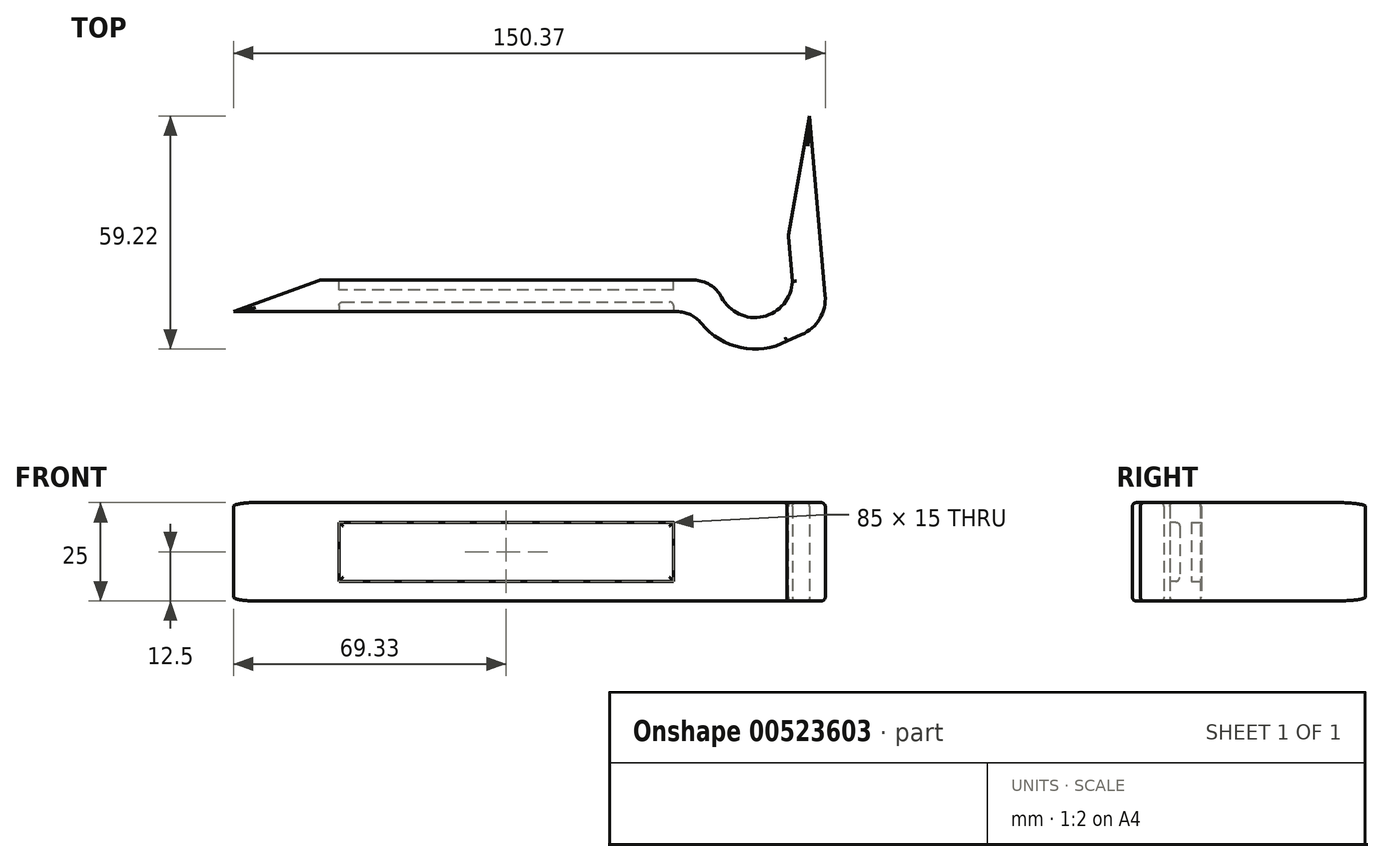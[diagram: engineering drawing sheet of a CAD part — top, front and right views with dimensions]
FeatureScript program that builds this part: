
annotation { "Feature Type Name" : "Feature", "Feature Type Description" : "" }
export const myFeature = defineFeature(function(context is Context, id is Id, definition is map)
    precondition{}
    {
        {
            var Q0;
            Q0=qCreatedBy(makeId("Top.planeOp"),FACE);
            var sketch = newSketch(context, id + "F0", { "sketchPlane" : qUnion([Q0])});
            skLineSegment(sketch, "E0.bottom", {"start": v(-48.85, 1.55) * mm, "end": v(46.1, 1.55) * mm});
            skLineSegment(sketch, "E0.top", {"start": v(-70.83, -6.45) * mm, "end": v(41.82, -6.45) * mm});
            skLineSegment(sketch, "E1", {"start": v(-70.83, -6.45) * mm, "end": v(-48.85, 1.55) * mm});
            skArc(sketch, "E2", {"start": v(48.05, -9.43) * mm, "mid": v(58.13, -15.59) * mm, "end": v(69.83, -13.93) * mm});
            skArc(sketch, "E3.0", {"start": v(53.22, -2.8) * mm, "mid": v(63.9, -7.68) * mm, "end": v(71.17, 1.55) * mm});
            skPoint(sketch, "E4.visualSharp", {"position": v(52.17, 1.55) * mm});
            skArc(sketch, "E4.filletArc", {"start": v(53.22, -2.8) * mm, "mid": v(50.28, 0.38) * mm, "end": v(46.1, 1.55) * mm});
            skArc(sketch, "E5.filletArc", {"start": v(48.05, -9.43) * mm, "mid": v(45.27, -7.23) * mm, "end": v(41.82, -6.45) * mm});
            skLineSegment(sketch, "E6", {"start": v(79.5, -2.27) * mm, "end": v(75.52, 43.27) * mm});
            skLineSegment(sketch, "E7", {"start": v(67.5, -14.95) * mm, "end": v(73.55, -12.3) * mm});
            skLineSegment(sketch, "E8.0", {"start": v(71.17, 1.25) * mm, "end": v(70.15, 12.83) * mm});
            skPoint(sketch, "E9.visualSharp", {"position": v(80.13, -9.43) * mm});
            skArc(sketch, "E9.filletArc", {"start": v(73.55, -12.3) * mm, "mid": v(78.14, -8.25) * mm, "end": v(79.5, -2.27) * mm});
            skLineSegment(sketch, "E10", {"start": v(75.52, 43.27) * mm, "end": v(70.15, 12.83) * mm});
            skSolve(sketch);
        }
        {
            var Q0;
            Q0 = qSketchRegion(id + "F0", true);
            extrude(context, id + "F1", {"entities" : qUnion([Q0]), "depth" : 25 * mm, "offsetDistance" : 25 * mm});
        }
        {
            var Q0;
            Q0=makeQuery(id+"F1.opExtrude","SWEPT_FACE",FACE,{"disambiguationData":[OSD([sQuery(id+"F0.wireOp",EDGE,"E0.bottom")])]});
            var sketch = newSketch(context, id + "F2", { "sketchPlane" : qUnion([Q0])});
            skLineSegment(sketch, "E11.0", {"start": v(-41, 20) * mm, "end": v(44, 20) * mm});
            skLineSegment(sketch, "E11.1", {"start": v(-41, 20) * mm, "end": v(-41, 5) * mm});
            skLineSegment(sketch, "E11.2", {"start": v(-41, 5) * mm, "end": v(44, 5) * mm});
            skLineSegment(sketch, "E11.3", {"start": v(44, 20) * mm, "end": v(44, 5) * mm});
            skSolve(sketch);
        }
        {
            var Q0;
            Q0 = qSketchRegion(id + "F2", true);
            extrude(context, id + "F3", {"entities" : qUnion([Q0]), "operationType" : NewBodyOperationType.REMOVE, "oppositeDirection" : true, "depth" : 2.5 * mm, "offsetDistance" : 25 * mm});
        }
        {
            var Q0;
            Q0=makeQuery(id+"F1.opExtrude","SWEPT_FACE",FACE,{"disambiguationData":[OSD([sQuery(id+"F0.wireOp",EDGE,"E0.top")])]});
            var sketch = newSketch(context, id + "F4", { "sketchPlane" : qUnion([Q0])});
            skLineSegment(sketch, "E12.bottom", {"start": v(-44, 20) * mm, "end": v(41, 20) * mm});
            skLineSegment(sketch, "E12.top", {"start": v(-44, 5) * mm, "end": v(41, 5) * mm});
            skLineSegment(sketch, "E12.left", {"start": v(-44, 20) * mm, "end": v(-44, 5) * mm});
            skLineSegment(sketch, "E12.right", {"start": v(41, 20) * mm, "end": v(41, 5) * mm});
            skSolve(sketch);
        }
        {
            var Q0;
            Q0 = qSketchRegion(id + "F4", true);
            extrude(context, id + "F5", {"entities" : qUnion([Q0]), "operationType" : NewBodyOperationType.REMOVE, "oppositeDirection" : true, "depth" : 2.5 * mm, "offsetDistance" : 25 * mm});
        }
        {
            var Q0;
            Q0=makeQuery(id+"F1.opExtrude","CAP_EDGE",EDGE,{"disambiguationData":[OSD([sQuery(id+"F0.wireOp",EDGE,"E0.bottom")])],"isStart":true});
            var Q1;
            Q1=makeQuery(id+"F1.opExtrude","CAP_EDGE",EDGE,{"disambiguationData":[OSD([sQuery(id+"F0.wireOp",EDGE,"E8.0")])],"isStart":true});
            var Q2;
            Q2=makeQuery(id+"F1.opExtrude","SWEPT_EDGE",EDGE,{"disambiguationData":[OSD([sQuery(id+"F0.wireOp",EDGE,"E8.0"),sQuery(id+"F0.wireOp",EDGE,"E10")])]});
            var Q3;
            Q3=makeQuery(id+"F1.opExtrude","CAP_EDGE",EDGE,{"disambiguationData":[OSD([sQuery(id+"F0.wireOp",EDGE,"E8.0")])],"isStart":false});
            var Q4;
            Q4=makeQuery(id+"F1.opExtrude","CAP_EDGE",EDGE,{"disambiguationData":[OSD([sQuery(id+"F0.wireOp",EDGE,"E3.0")])],"isStart":false});
            var Q5;
            Q5=makeQuery(id+"F1.opExtrude","SWEPT_EDGE",EDGE,{"disambiguationData":[OSD([sQuery(id+"F0.wireOp",EDGE,"E0.bottom"),sQuery(id+"F0.wireOp",EDGE,"E1")])]});
            var Q6;
            Q6=makeQuery(id+"F3.boolean.opBoolean","COPY",EDGE,{"derivedFrom":makeQuery(id+"F3.opExtrude","CAP_EDGE",EDGE,{"disambiguationData":[OSD([sQuery(id+"F2.wireOp",EDGE,"E11.3")])],"isStart":true})});
            var Q7;
            Q7=makeQuery(id+"F3.boolean.opBoolean","COPY",EDGE,{"derivedFrom":makeQuery(id+"F3.opExtrude","CAP_EDGE",EDGE,{"disambiguationData":[OSD([sQuery(id+"F2.wireOp",EDGE,"E11.2")])],"isStart":true})});
            var Q8;
            Q8=makeQuery(id+"F3.boolean.opBoolean","COPY",EDGE,{"derivedFrom":makeQuery(id+"F3.opExtrude","CAP_EDGE",EDGE,{"disambiguationData":[OSD([sQuery(id+"F2.wireOp",EDGE,"E11.1")])],"isStart":true})});
            var Q9;
            Q9=makeQuery(id+"F3.boolean.opBoolean","COPY",EDGE,{"derivedFrom":makeQuery(id+"F3.opExtrude","CAP_EDGE",EDGE,{"disambiguationData":[OSD([sQuery(id+"F2.wireOp",EDGE,"E11.0")])],"isStart":true})});
            var Q10;
            Q10=makeQuery(id+"F1.opExtrude","CAP_EDGE",EDGE,{"disambiguationData":[OSD([sQuery(id+"F0.wireOp",EDGE,"E0.top")])],"isStart":false});
            var Q11;
            Q11=makeQuery(id+"F1.opExtrude","CAP_EDGE",EDGE,{"disambiguationData":[OSD([sQuery(id+"F0.wireOp",EDGE,"E1")])],"isStart":true});
            var Q12;
            Q12=makeQuery(id+"F1.opExtrude","CAP_EDGE",EDGE,{"disambiguationData":[OSD([sQuery(id+"F0.wireOp",EDGE,"E1")])],"isStart":false});
            var Q13;
            Q13=makeQuery(id+"F1.opExtrude","CAP_EDGE",EDGE,{"disambiguationData":[OSD([sQuery(id+"F0.wireOp",EDGE,"E0.top")])],"isStart":true});
            var Q14;
            Q14=makeQuery(id+"F5.boolean.opBoolean","COPY",EDGE,{"derivedFrom":makeQuery(id+"F5.opExtrude","CAP_EDGE",EDGE,{"disambiguationData":[OSD([sQuery(id+"F4.wireOp",EDGE,"E12.top")])],"isStart":true})});
            var Q15;
            Q15=makeQuery(id+"F1.opExtrude","CAP_EDGE",EDGE,{"disambiguationData":[OSD([sQuery(id+"F0.wireOp",EDGE,"E10")])],"isStart":true});
            var Q16;
            Q16=makeQuery(id+"F1.opExtrude","CAP_EDGE",EDGE,{"disambiguationData":[OSD([sQuery(id+"F0.wireOp",EDGE,"E10")])],"isStart":false});
            var Q17;
            Q17=makeQuery(id+"F5.boolean.opBoolean","COPY",EDGE,{"derivedFrom":makeQuery(id+"F5.opExtrude","CAP_EDGE",EDGE,{"disambiguationData":[OSD([sQuery(id+"F4.wireOp",EDGE,"E12.bottom")])],"isStart":true})});
            var Q18;
            Q18=makeQuery(id+"F5.boolean.opBoolean","COPY",EDGE,{"derivedFrom":makeQuery(id+"F5.opExtrude","CAP_EDGE",EDGE,{"disambiguationData":[OSD([sQuery(id+"F4.wireOp",EDGE,"E12.bottom")])],"isStart":false})});
            var Q19;
            Q19=makeQuery(id+"F5.boolean.opBoolean","COPY",EDGE,{"derivedFrom":makeQuery(id+"F5.opExtrude","CAP_EDGE",EDGE,{"disambiguationData":[OSD([sQuery(id+"F4.wireOp",EDGE,"E12.top")])],"isStart":false})});
            var Q20;
            Q20=makeQuery(id+"F5.boolean.opBoolean","COPY",EDGE,{"derivedFrom":makeQuery(id+"F5.opExtrude","CAP_EDGE",EDGE,{"disambiguationData":[OSD([sQuery(id+"F4.wireOp",EDGE,"E12.right")])],"isStart":false})});
            var Q21;
            Q21=makeQuery(id+"F5.boolean.opBoolean","COPY",EDGE,{"derivedFrom":makeQuery(id+"F5.opExtrude","CAP_EDGE",EDGE,{"disambiguationData":[OSD([sQuery(id+"F4.wireOp",EDGE,"E12.left")])],"isStart":false})});
            var Q22;
            Q22=makeQuery(id+"F5.boolean.opBoolean","COPY",EDGE,{"derivedFrom":makeQuery(id+"F5.opExtrude","CAP_EDGE",EDGE,{"disambiguationData":[OSD([sQuery(id+"F4.wireOp",EDGE,"E12.left")])],"isStart":true})});
            var Q23;
            Q23=makeQuery(id+"F1.opExtrude","CAP_EDGE",EDGE,{"disambiguationData":[OSD([sQuery(id+"F0.wireOp",EDGE,"E6")])],"isStart":true});
            var Q24;
            Q24=makeQuery(id+"F1.opExtrude","CAP_EDGE",EDGE,{"disambiguationData":[OSD([sQuery(id+"F0.wireOp",EDGE,"E9.filletArc")])],"isStart":true});
            var Q25;
            Q25=makeQuery(id+"F1.opExtrude","CAP_EDGE",EDGE,{"disambiguationData":[OSD([sQuery(id+"F0.wireOp",EDGE,"E9.filletArc")])],"isStart":false});
            fillet(context, id + "F6", {"entities" : qUnion([Q0, Q1, Q2, Q3, Q4, Q5, Q6, Q7, Q8, Q9, Q10, Q11, Q12, Q13, Q14, Q15, Q16, Q17, Q18, Q19, Q20, Q21, Q22, Q23, Q24, Q25]), "radius" : 1 * mm, "tangentPropagation" : true, "allowEdgeOverflow" : false});
        }
    });
